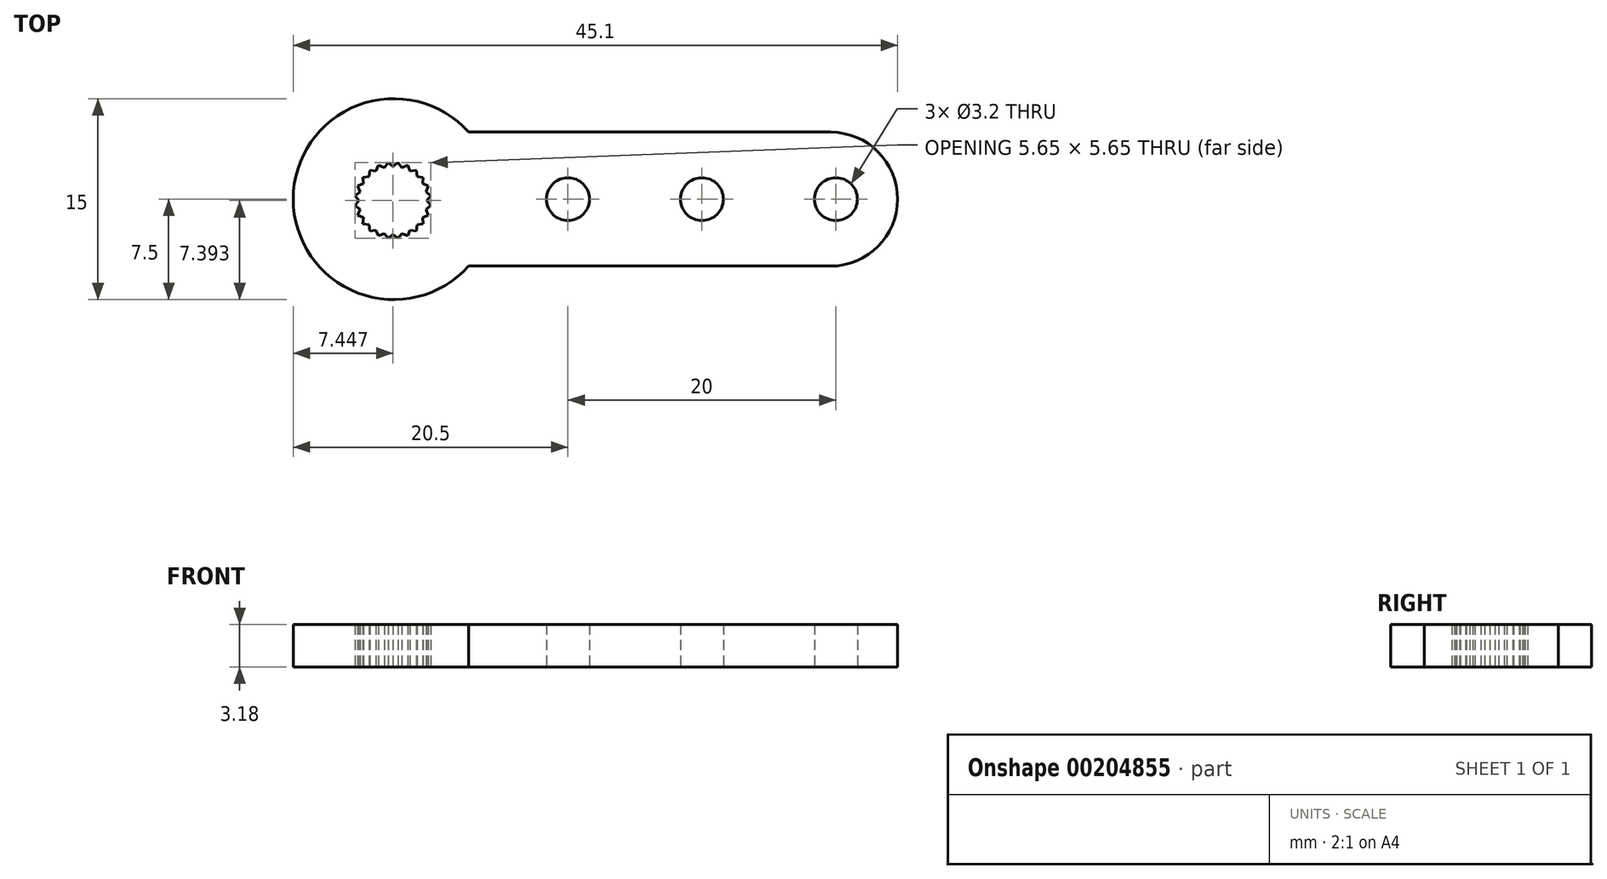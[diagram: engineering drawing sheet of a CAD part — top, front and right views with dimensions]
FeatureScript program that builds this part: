
annotation { "Feature Type Name" : "Feature", "Feature Type Description" : "" }
export const myFeature = defineFeature(function(context is Context, id is Id, definition is map)
    precondition{}
    {
        {
            var Q0;
            Q0=qCreatedBy(makeId("Top.planeOp"),FACE);
            var sketch = newSketch(context, id + "F0", { "sketchPlane" : qUnion([Q0])});
            skLineSegment(sketch, "E0.MirrorCS", {"start": v(5.6, 5) * mm, "end": v(32.6, 5) * mm});
            skLineSegment(sketch, "E1.MirrorCS", {"start": v(5.6, -5) * mm, "end": v(32.6, -5) * mm});
            skArc(sketch, "E2.MirrorCS", {"start": v(32.6, -5) * mm, "mid": v(36.14, -3.54) * mm, "end": v(37.6, 0) * mm});
            skCircle(sketch, "E3.MirrorC", {"center": v(23, 0) * mm, "radius": 1.6 * mm});
            skCircle(sketch, "E4.MirrorC", {"center": v(33, 0) * mm, "radius": 1.6 * mm});
            skCircle(sketch, "E5.MirrorC", {"center": v(13, 0) * mm, "radius": 1.6 * mm});
            skArc(sketch, "E6.MirrorCS", {"start": v(32.6, 5) * mm, "mid": v(36.14, 3.54) * mm, "end": v(37.6, 0) * mm});
            skLineSegment(sketch, "E7.MirrorCS", {"start": v(33, 0) * mm, "end": v(23, 0) * mm, "construction": true});
            skPoint(sketch, "E8.orphan", {"position": v(0, 5) * mm});
            skPoint(sketch, "E9.orphan", {"position": v(0, -5) * mm});
            skArc(sketch, "E10", {"start": v(5.6, 5) * mm, "mid": v(-7.5, 0) * mm, "end": v(5.6, -5) * mm});
            skPoint(sketch, "E11", {"position": v(-0.05, 2.43) * mm});
            skPoint(sketch, "E12", {"position": v(0.32, 2.72) * mm});
            skLineSegment(sketch, "E13", {"start": v(-0.05, 2.43) * mm, "end": v(0.32, 2.72) * mm});
            skLineSegment(sketch, "E14", {"start": v(-0.05, 2.43) * mm, "end": v(-0.42, 2.72) * mm});
            skLineSegment(sketch, "E15", {"start": v(0.32, 2.72) * mm, "end": v(0.6, 2.35) * mm});
            skLineSegment(sketch, "E16", {"start": v(0.6, 2.35) * mm, "end": v(1.04, 2.53) * mm});
            skLineSegment(sketch, "E17", {"start": v(1.22, 2.1) * mm, "end": v(1.04, 2.53) * mm});
            skLineSegment(sketch, "E18", {"start": v(1.68, 2.15) * mm, "end": v(1.22, 2.1) * mm});
            skLineSegment(sketch, "E19", {"start": v(1.74, 1.69) * mm, "end": v(1.68, 2.15) * mm});
            skLineSegment(sketch, "E20", {"start": v(2.2, 1.63) * mm, "end": v(1.74, 1.69) * mm});
            skLineSegment(sketch, "E21", {"start": v(2.15, 1.16) * mm, "end": v(2.2, 1.63) * mm});
            skLineSegment(sketch, "E22", {"start": v(2.15, 1.16) * mm, "end": v(2.58, 0.98) * mm});
            skLineSegment(sketch, "E23", {"start": v(2.58, 0.98) * mm, "end": v(2.4, 0.55) * mm});
            skLineSegment(sketch, "E24", {"start": v(2.4, 0.55) * mm, "end": v(2.77, 0.27) * mm});
            skLineSegment(sketch, "E25", {"start": v(2.77, 0.27) * mm, "end": v(2.49, -0.1) * mm});
            skLineSegment(sketch, "E26", {"start": v(2.49, -0.1) * mm, "end": v(2.77, -0.48) * mm});
            skLineSegment(sketch, "E27", {"start": v(2.77, -0.48) * mm, "end": v(2.4, -0.76) * mm});
            skLineSegment(sketch, "E28", {"start": v(2.4, -0.76) * mm, "end": v(2.58, -1.2) * mm});
            skLineSegment(sketch, "E29", {"start": v(2.58, -1.2) * mm, "end": v(2.15, -1.38) * mm});
            skLineSegment(sketch, "E30", {"start": v(2.15, -1.38) * mm, "end": v(2.2, -1.84) * mm});
            skLineSegment(sketch, "E31", {"start": v(2.2, -1.84) * mm, "end": v(1.74, -1.9) * mm});
            skLineSegment(sketch, "E32", {"start": v(1.74, -1.9) * mm, "end": v(1.68, -2.37) * mm});
            skLineSegment(sketch, "E33", {"start": v(1.68, -2.37) * mm, "end": v(1.22, -2.3) * mm});
            skLineSegment(sketch, "E34", {"start": v(1.22, -2.3) * mm, "end": v(1.04, -2.74) * mm});
            skLineSegment(sketch, "E35", {"start": v(1.04, -2.74) * mm, "end": v(0.6, -2.56) * mm});
            skLineSegment(sketch, "E36", {"start": v(0.6, -2.56) * mm, "end": v(0.32, -2.93) * mm});
            skLineSegment(sketch, "E37", {"start": v(0.32, -2.93) * mm, "end": v(-0.05, -2.65) * mm});
            skLineSegment(sketch, "E38", {"start": v(-0.05, -2.65) * mm, "end": v(-0.42, -2.93) * mm});
            skLineSegment(sketch, "E39", {"start": v(-0.42, -2.93) * mm, "end": v(-0.71, -2.56) * mm});
            skLineSegment(sketch, "E40", {"start": v(-0.71, -2.56) * mm, "end": v(-1.14, -2.74) * mm});
            skLineSegment(sketch, "E41", {"start": v(-1.14, -2.74) * mm, "end": v(-1.32, -2.3) * mm});
            skLineSegment(sketch, "E42", {"start": v(-1.32, -2.3) * mm, "end": v(-1.79, -2.37) * mm});
            skLineSegment(sketch, "E43", {"start": v(-1.79, -2.37) * mm, "end": v(-1.85, -1.9) * mm});
            skLineSegment(sketch, "E44", {"start": v(-1.85, -1.9) * mm, "end": v(-2.31, -1.84) * mm});
            skLineSegment(sketch, "E45", {"start": v(-2.31, -1.84) * mm, "end": v(-2.25, -1.38) * mm});
            skLineSegment(sketch, "E46", {"start": v(-2.69, -1.2) * mm, "end": v(-2.25, -1.38) * mm});
            skLineSegment(sketch, "E47", {"start": v(-2.69, -1.2) * mm, "end": v(-2.5, -0.76) * mm});
            skLineSegment(sketch, "E48", {"start": v(-2.5, -0.76) * mm, "end": v(-2.88, -0.48) * mm});
            skLineSegment(sketch, "E49", {"start": v(-2.88, -0.48) * mm, "end": v(-2.6, -0.1) * mm});
            skLineSegment(sketch, "E50", {"start": v(-2.6, -0.1) * mm, "end": v(-2.88, 0.27) * mm});
            skLineSegment(sketch, "E51", {"start": v(-2.88, 0.27) * mm, "end": v(-2.5, 0.55) * mm});
            skLineSegment(sketch, "E52", {"start": v(-2.69, 0.98) * mm, "end": v(-2.5, 0.55) * mm});
            skLineSegment(sketch, "E53", {"start": v(-2.25, 1.16) * mm, "end": v(-2.69, 0.98) * mm});
            skLineSegment(sketch, "E54", {"start": v(-2.31, 1.63) * mm, "end": v(-2.25, 1.16) * mm});
            skLineSegment(sketch, "E55", {"start": v(-2.31, 1.63) * mm, "end": v(-1.85, 1.69) * mm});
            skLineSegment(sketch, "E56", {"start": v(-1.85, 1.69) * mm, "end": v(-1.79, 2.15) * mm});
            skLineSegment(sketch, "E57", {"start": v(-1.79, 2.15) * mm, "end": v(-1.32, 2.1) * mm});
            skLineSegment(sketch, "E58", {"start": v(-1.32, 2.1) * mm, "end": v(-1.14, 2.53) * mm});
            skLineSegment(sketch, "E59", {"start": v(-1.14, 2.53) * mm, "end": v(-0.71, 2.35) * mm});
            skLineSegment(sketch, "E60", {"start": v(-0.71, 2.35) * mm, "end": v(-0.42, 2.72) * mm});
            skSolve(sketch);
        }
        {
            var Q0;
            Q0=makeQuery(id+"F0.imprint","IMPRINT",FACE,{"disambiguationData":[TD([[makeQuery(id+"F0.imprint","IMPRINT",EDGE,{"derivedFrom":sQuery(id+"F0.wireOp",EDGE,"1ef719ea-a875-445d-944f-9bdb62d9089b7.MirrorC")}),-1.0]])]});
            var Q1;
            Q1=makeQuery(id+"F0.imprint","IMPRINT",FACE,{"disambiguationData":[TD([[makeQuery(id+"F0.imprint","IMPRINT",EDGE,{"derivedFrom":sQuery(id+"F0.wireOp",EDGE,"E3.MirrorC")}),-1.0]])]});
            extrude(context, id + "F1", {"entities" : qUnion([Q0, Q1]), "depth" : 3.17 * mm});
        }
    });
